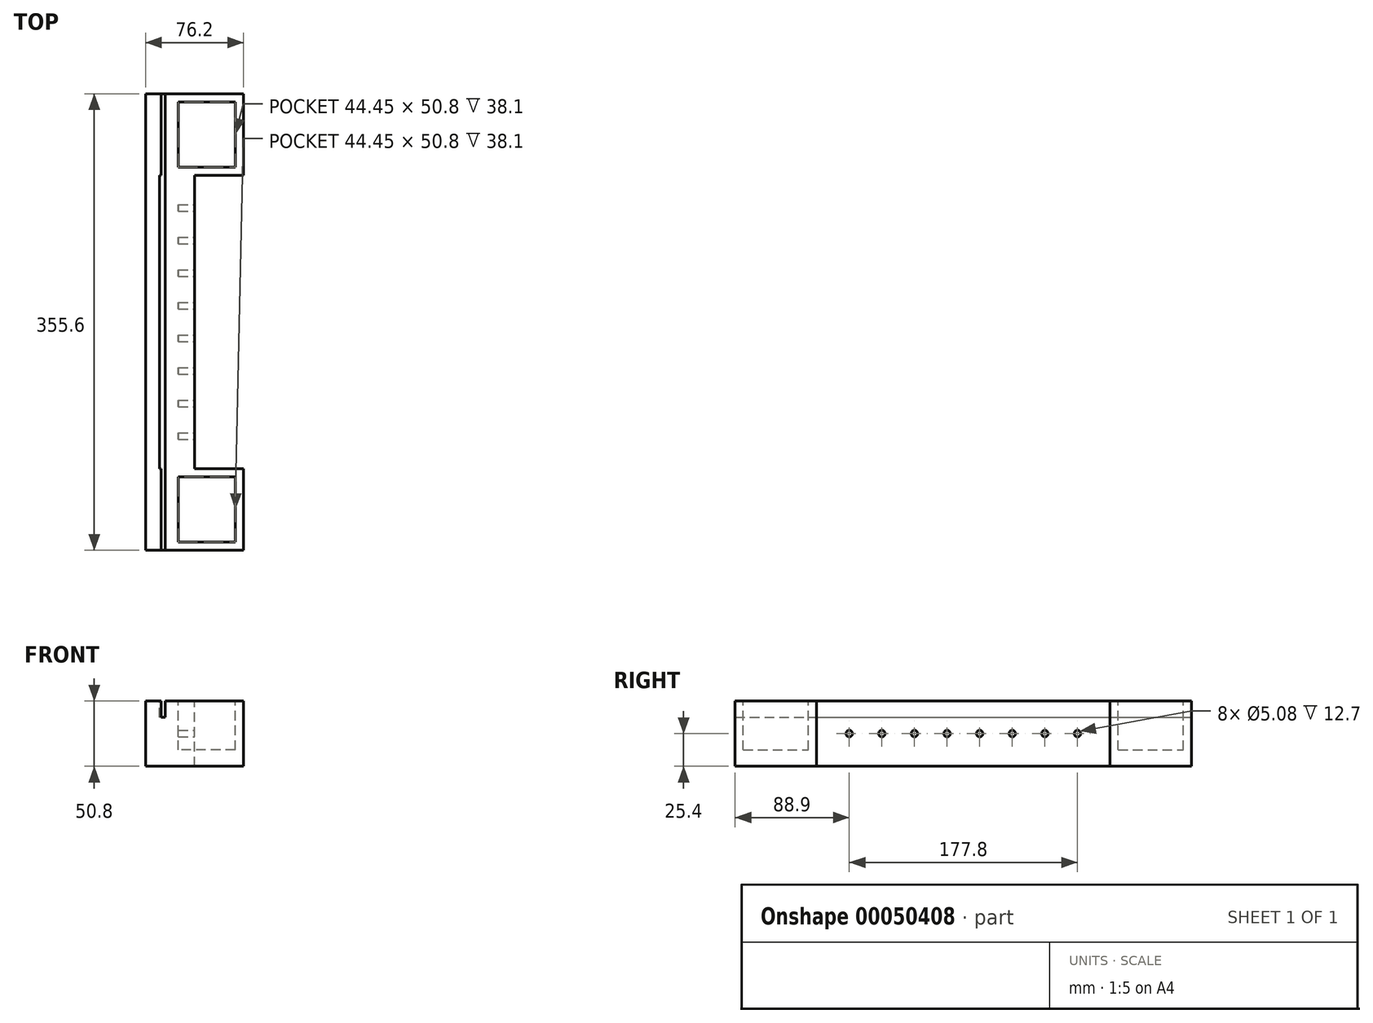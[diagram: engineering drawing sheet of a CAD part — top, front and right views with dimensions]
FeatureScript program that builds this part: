
annotation { "Feature Type Name" : "Feature", "Feature Type Description" : "" }
export const myFeature = defineFeature(function(context is Context, id is Id, definition is map)
    precondition{}
    {
        {
            var Q0;
            Q0=qCreatedBy(makeId("Right.planeOp"),FACE);
            var sketch = newSketch(context, id + "F0", { "sketchPlane" : qUnion([Q0])});
            skLineSegment(sketch, "E0.bottom", {"start": v(0, 0) * mm, "end": v(368.3, 0) * mm});
            skLineSegment(sketch, "E0.top", {"start": v(0, 50.8) * mm, "end": v(368.3, 50.8) * mm});
            skLineSegment(sketch, "E0.left", {"start": v(0, 0) * mm, "end": v(0, 50.8) * mm});
            skLineSegment(sketch, "E0.right", {"start": v(368.3, 0) * mm, "end": v(368.3, 50.8) * mm});
            skSolve(sketch);
        }
        {
            var Q0;
            Q0=makeQuery(id+"F0.imprint","IMPRINT",FACE,{"disambiguationData":[TD([[makeQuery(id+"F0.imprint","IMPRINT",EDGE,{"derivedFrom":sQuery(id+"F0.wireOp",EDGE,"E0.bottom")}),1.0]])]});
            extrude(context, id + "F1", {"entities" : qUnion([Q0]), "depth" : 38.1 * mm});
        }
        {
            var Q0;
            Q0=makeQuery(id+"F1.opExtrude","CAP_FACE",FACE,{"disambiguationData":[OSD([sQuery(id+"F0.wireOp",EDGE,"E0.bottom"),sQuery(id+"F0.wireOp",EDGE,"E0.top"),sQuery(id+"F0.wireOp",EDGE,"E0.left"),sQuery(id+"F0.wireOp",EDGE,"E0.right")])],"isStart":false});
            var sketch = newSketch(context, id + "F2", { "sketchPlane" : qUnion([Q0])});
            skLineSegment(sketch, "E1.bottom", {"start": v(0, 0) * mm, "end": v(76.2, 0) * mm});
            skLineSegment(sketch, "E1.top", {"start": v(0, 50.8) * mm, "end": v(76.2, 50.8) * mm});
            skLineSegment(sketch, "E1.left", {"start": v(0, 0) * mm, "end": v(0, 50.8) * mm});
            skLineSegment(sketch, "E1.right", {"start": v(76.2, 0) * mm, "end": v(76.2, 50.8) * mm});
            skLineSegment(sketch, "E2.bottom", {"start": v(368.3, 0) * mm, "end": v(292.1, 0) * mm});
            skLineSegment(sketch, "E2.top", {"start": v(368.3, 50.8) * mm, "end": v(292.1, 50.8) * mm});
            skLineSegment(sketch, "E2.left", {"start": v(368.3, 0) * mm, "end": v(368.3, 50.8) * mm});
            skLineSegment(sketch, "E2.right", {"start": v(292.1, 0) * mm, "end": v(292.1, 50.8) * mm});
            skSolve(sketch);
        }
        {
            var Q0;
            Q0=makeQuery(id+"F2.imprint","IMPRINT",FACE,{"disambiguationData":[TD([[makeQuery(id+"F2.imprint","IMPRINT",EDGE,{"derivedFrom":sQuery(id+"F2.wireOp",EDGE,"E1.bottom")}),1.0]])]});
            var Q1;
            Q1=makeQuery(id+"F2.imprint","IMPRINT",FACE,{"disambiguationData":[TD([[makeQuery(id+"F2.imprint","IMPRINT",EDGE,{"derivedFrom":sQuery(id+"F2.wireOp",EDGE,"E2.bottom")}),1.0]])]});
            extrude(context, id + "F3", {"entities" : qUnion([Q0, Q1]), "operationType" : NewBodyOperationType.ADD, "depth" : 38.1 * mm});
        }
        {
            var Q0;
            Q0=makeQuery(id+"F3.boolean.opBoolean","MERGE",FACE,{"derivedFrom":[makeQuery(id+"F1.opExtrude","SWEPT_FACE",FACE,{"disambiguationData":[OSD([sQuery(id+"F0.wireOp",EDGE,"E0.top")])]}),makeQuery(id+"F3.opExtrude","SWEPT_FACE",FACE,{"disambiguationData":[OSD([sQuery(id+"F2.wireOp",EDGE,"E1.top")])]}),makeQuery(id+"F3.opExtrude","SWEPT_FACE",FACE,{"disambiguationData":[OSD([sQuery(id+"F2.wireOp",EDGE,"E2.top")])]})]});
            var sketch = newSketch(context, id + "F4", { "sketchPlane" : qUnion([Q0])});
            skLineSegment(sketch, "E3.bottom", {"start": v(11.96, 6.35) * mm, "end": v(15.14, 6.35) * mm});
            skLineSegment(sketch, "E3.top", {"start": v(11.96, 69.85) * mm, "end": v(15.14, 69.85) * mm});
            skLineSegment(sketch, "E3.left", {"start": v(11.96, 6.35) * mm, "end": v(11.96, 69.85) * mm});
            skLineSegment(sketch, "E3.right", {"start": v(15.14, 6.35) * mm, "end": v(15.14, 69.85) * mm});
            skLineSegment(sketch, "E4.bottom", {"start": v(11.96, 298.45) * mm, "end": v(15.14, 298.45) * mm});
            skLineSegment(sketch, "E4.top", {"start": v(11.96, 361.95) * mm, "end": v(15.14, 361.95) * mm});
            skLineSegment(sketch, "E4.left", {"start": v(11.96, 298.45) * mm, "end": v(11.96, 361.95) * mm});
            skLineSegment(sketch, "E4.right", {"start": v(15.14, 298.45) * mm, "end": v(15.14, 361.95) * mm});
            skLineSegment(sketch, "E5.bottom", {"start": v(15.14, 69.85) * mm, "end": v(10.9, 69.85) * mm});
            skLineSegment(sketch, "E5.top", {"start": v(15.14, 298.45) * mm, "end": v(10.9, 298.45) * mm});
            skLineSegment(sketch, "E5.left", {"start": v(15.14, 69.85) * mm, "end": v(15.14, 298.45) * mm});
            skLineSegment(sketch, "E5.right", {"start": v(10.9, 69.85) * mm, "end": v(10.9, 298.45) * mm});
            skSolve(sketch);
        }
        {
            var Q0;
            Q0=makeQuery(id+"F4.imprint","IMPRINT",FACE,{"disambiguationData":[TD([[makeQuery(id+"F4.imprint","IMPRINT",EDGE,{"derivedFrom":sQuery(id+"F4.wireOp",EDGE,"E3.bottom")}),1.0]])]});
            var Q1;
            Q1=makeQuery(id+"F4.imprint","IMPRINT",FACE,{"disambiguationData":[TD([[makeQuery(id+"F4.imprint","IMPRINT",EDGE,{"derivedFrom":sQuery(id+"F4.wireOp",EDGE,"E4.top")}),-1.0]])]});
            var Q2;
            {var subQ3=sQuery(id+"F4.wireOp",EDGE,"E5.left");Q2=makeQuery(id+"F4.imprint","IMPRINT",FACE,{"disambiguationData":[TD([[makeQuery(id+"F4.imprint","IMPRINT",EDGE,{"derivedFrom":subQ3}),1.0]])]});}
            extrude(context, id + "F5", {"entities" : qUnion([Q0, Q1, Q2]), "operationType" : NewBodyOperationType.REMOVE, "oppositeDirection" : true, "depth" : 12.7 * mm});
        }
        {
            var Q0;
            Q0=makeQuery(id+"F3.boolean.opBoolean","MERGE",FACE,{"derivedFrom":[makeQuery(id+"F1.opExtrude","SWEPT_FACE",FACE,{"disambiguationData":[OSD([sQuery(id+"F0.wireOp",EDGE,"E0.top")])]}),makeQuery(id+"F3.opExtrude","SWEPT_FACE",FACE,{"disambiguationData":[OSD([sQuery(id+"F2.wireOp",EDGE,"E1.top")])]}),makeQuery(id+"F3.opExtrude","SWEPT_FACE",FACE,{"disambiguationData":[OSD([sQuery(id+"F2.wireOp",EDGE,"E2.top")])]})]});
            var sketch = newSketch(context, id + "F6", { "sketchPlane" : qUnion([Q0])});
            skLineSegment(sketch, "E6.0.0", {"start": v(0, 368.3) * mm, "end": v(0, 0) * mm});
            skLineSegment(sketch, "E6.0.1", {"start": v(0, 0) * mm, "end": v(76.2, 0) * mm});
            skLineSegment(sketch, "E6.0.2", {"start": v(76.2, 0) * mm, "end": v(76.2, 76.2) * mm});
            skLineSegment(sketch, "E6.0.3", {"start": v(76.2, 76.2) * mm, "end": v(38.1, 76.2) * mm});
            skLineSegment(sketch, "E6.0.4", {"start": v(38.1, 76.2) * mm, "end": v(38.1, 292.1) * mm});
            skLineSegment(sketch, "E6.0.5", {"start": v(38.1, 292.1) * mm, "end": v(76.2, 292.1) * mm});
            skLineSegment(sketch, "E6.0.6", {"start": v(76.2, 292.1) * mm, "end": v(76.2, 368.3) * mm});
            skLineSegment(sketch, "E6.0.7", {"start": v(76.2, 368.3) * mm, "end": v(0, 368.3) * mm});
            skLineSegment(sketch, "E7.bottom", {"start": v(69.85, 12.7) * mm, "end": v(25.4, 12.7) * mm});
            skLineSegment(sketch, "E7.top", {"start": v(69.85, 63.5) * mm, "end": v(25.4, 63.5) * mm});
            skLineSegment(sketch, "E7.left", {"start": v(69.85, 12.7) * mm, "end": v(69.85, 63.5) * mm});
            skLineSegment(sketch, "E7.right", {"start": v(25.4, 12.7) * mm, "end": v(25.4, 63.5) * mm});
            skLineSegment(sketch, "E8.bottom", {"start": v(69.85, 304.8) * mm, "end": v(25.4, 304.8) * mm});
            skLineSegment(sketch, "E8.top", {"start": v(69.85, 355.6) * mm, "end": v(25.4, 355.6) * mm});
            skLineSegment(sketch, "E8.left", {"start": v(69.85, 304.8) * mm, "end": v(69.85, 355.6) * mm});
            skLineSegment(sketch, "E8.right", {"start": v(25.4, 304.8) * mm, "end": v(25.4, 355.6) * mm});
            skSolve(sketch);
        }
        {
            var Q0;
            Q0=makeQuery(id+"F6.imprint","IMPRINT",FACE,{"disambiguationData":[TD([[makeQuery(id+"F6.imprint","IMPRINT",EDGE,{"derivedFrom":sQuery(id+"F6.wireOp",EDGE,"E7.bottom")}),-1.0]])]});
            var Q1;
            Q1=makeQuery(id+"F6.imprint","IMPRINT",FACE,{"disambiguationData":[TD([[makeQuery(id+"F6.imprint","IMPRINT",EDGE,{"derivedFrom":sQuery(id+"F6.wireOp",EDGE,"E8.bottom")}),-1.0]])]});
            extrude(context, id + "F7", {"entities" : qUnion([Q0, Q1]), "operationType" : NewBodyOperationType.REMOVE, "oppositeDirection" : true, "depth" : 38.1 * mm});
        }
        {
            var Q0;
            Q0=makeQuery(id+"F1.opExtrude","CAP_FACE",FACE,{"disambiguationData":[OSD([sQuery(id+"F0.wireOp",EDGE,"E0.bottom"),sQuery(id+"F0.wireOp",EDGE,"E0.top"),sQuery(id+"F0.wireOp",EDGE,"E0.left"),sQuery(id+"F0.wireOp",EDGE,"E0.right")])],"isStart":false});
            var sketch = newSketch(context, id + "F8", { "sketchPlane" : qUnion([Q0])});
            skCircle(sketch, "E9", {"center": v(95.25, 25.4) * mm, "radius": 2.54 * mm});
            skCircle(sketch, "E10.1.0.0", {"center": v(120.65, 25.4) * mm, "radius": 2.54 * mm});
            skCircle(sketch, "E10.2.0.0", {"center": v(146.05, 25.4) * mm, "radius": 2.54 * mm});
            skCircle(sketch, "E10.3.0.0", {"center": v(171.45, 25.4) * mm, "radius": 2.54 * mm});
            skCircle(sketch, "E10.4.0.0", {"center": v(196.85, 25.4) * mm, "radius": 2.54 * mm});
            skCircle(sketch, "E10.5.0.0", {"center": v(222.25, 25.4) * mm, "radius": 2.54 * mm});
            skCircle(sketch, "E10.6.0.0", {"center": v(247.65, 25.4) * mm, "radius": 2.54 * mm});
            skLineSegment(sketch, "E10.direction1", {"start": v(95.25, 25.4) * mm, "end": v(120.65, 25.4) * mm, "construction": true});
            skCircle(sketch, "E11.0.7.0", {"center": v(273.05, 25.4) * mm, "radius": 2.54 * mm});
            skSolve(sketch);
        }
        {
            var Q0;
            Q0=makeQuery(id+"F8.imprint","IMPRINT",FACE,{"disambiguationData":[TD([[makeQuery(id+"F8.imprint","IMPRINT",EDGE,{"derivedFrom":sQuery(id+"F8.wireOp",EDGE,"E10.1.0.0")}),1.0]])]});
            var Q1;
            Q1=makeQuery(id+"F8.imprint","IMPRINT",FACE,{"disambiguationData":[TD([[makeQuery(id+"F8.imprint","IMPRINT",EDGE,{"derivedFrom":sQuery(id+"F8.wireOp",EDGE,"E10.2.0.0")}),1.0]])]});
            var Q2;
            Q2=makeQuery(id+"F8.imprint","IMPRINT",FACE,{"disambiguationData":[TD([[makeQuery(id+"F8.imprint","IMPRINT",EDGE,{"derivedFrom":sQuery(id+"F8.wireOp",EDGE,"E10.3.0.0")}),1.0]])]});
            var Q3;
            Q3=makeQuery(id+"F8.imprint","IMPRINT",FACE,{"disambiguationData":[TD([[makeQuery(id+"F8.imprint","IMPRINT",EDGE,{"derivedFrom":sQuery(id+"F8.wireOp",EDGE,"E10.4.0.0")}),1.0]])]});
            var Q4;
            Q4=makeQuery(id+"F8.imprint","IMPRINT",FACE,{"disambiguationData":[TD([[makeQuery(id+"F8.imprint","IMPRINT",EDGE,{"derivedFrom":sQuery(id+"F8.wireOp",EDGE,"E10.5.0.0")}),1.0]])]});
            var Q5;
            Q5=makeQuery(id+"F8.imprint","IMPRINT",FACE,{"disambiguationData":[TD([[makeQuery(id+"F8.imprint","IMPRINT",EDGE,{"derivedFrom":sQuery(id+"F8.wireOp",EDGE,"E10.6.0.0")}),1.0]])]});
            var Q6;
            Q6=makeQuery(id+"F8.imprint","IMPRINT",FACE,{"disambiguationData":[TD([[makeQuery(id+"F8.imprint","IMPRINT",EDGE,{"derivedFrom":sQuery(id+"F8.wireOp",EDGE,"E9")}),1.0]])]});
            var Q7;
            Q7=makeQuery(id+"F8.imprint","IMPRINT",FACE,{"disambiguationData":[TD([[makeQuery(id+"F8.imprint","IMPRINT",EDGE,{"derivedFrom":sQuery(id+"F8.wireOp",EDGE,"E11.0.7.0")}),1.0]])]});
            extrude(context, id + "F9", {"entities" : qUnion([Q0, Q1, Q2, Q3, Q4, Q5, Q6, Q7]), "operationType" : NewBodyOperationType.REMOVE, "oppositeDirection" : true, "depth" : 12.7 * mm});
        }
        {
            var Q0;
            Q0=makeQuery(id+"F3.boolean.opBoolean","MERGE",FACE,{"derivedFrom":[makeQuery(id+"F1.opExtrude","SWEPT_FACE",FACE,{"disambiguationData":[OSD([sQuery(id+"F0.wireOp",EDGE,"E0.top")])]}),makeQuery(id+"F3.opExtrude","SWEPT_FACE",FACE,{"disambiguationData":[OSD([sQuery(id+"F2.wireOp",EDGE,"E1.top")])]}),makeQuery(id+"F3.opExtrude","SWEPT_FACE",FACE,{"disambiguationData":[OSD([sQuery(id+"F2.wireOp",EDGE,"E2.top")])]})]});
            var sketch = newSketch(context, id + "F10", { "sketchPlane" : qUnion([Q0])});
            skLineSegment(sketch, "E12.bottom", {"start": v(0, 0) * mm, "end": v(76.2, 0) * mm});
            skLineSegment(sketch, "E12.top", {"start": v(0, 6.35) * mm, "end": v(76.2, 6.35) * mm});
            skLineSegment(sketch, "E12.left", {"start": v(0, 0) * mm, "end": v(0, 6.35) * mm});
            skLineSegment(sketch, "E12.right", {"start": v(76.2, 0) * mm, "end": v(76.2, 6.35) * mm});
            skLineSegment(sketch, "E13.bottom", {"start": v(38.1, 76.2) * mm, "end": v(76.2, 76.2) * mm});
            skLineSegment(sketch, "E13.top", {"start": v(38.1, 69.85) * mm, "end": v(76.2, 69.85) * mm});
            skLineSegment(sketch, "E13.left", {"start": v(38.1, 76.2) * mm, "end": v(38.1, 69.85) * mm});
            skLineSegment(sketch, "E13.right", {"start": v(76.2, 76.2) * mm, "end": v(76.2, 69.85) * mm});
            skLineSegment(sketch, "E14.bottom", {"start": v(0, 368.3) * mm, "end": v(76.2, 368.3) * mm});
            skLineSegment(sketch, "E14.top", {"start": v(0, 361.95) * mm, "end": v(76.2, 361.95) * mm});
            skLineSegment(sketch, "E14.left", {"start": v(0, 368.3) * mm, "end": v(0, 361.95) * mm});
            skLineSegment(sketch, "E14.right", {"start": v(76.2, 368.3) * mm, "end": v(76.2, 361.95) * mm});
            skLineSegment(sketch, "E15.bottom", {"start": v(38.1, 292.1) * mm, "end": v(76.2, 292.1) * mm});
            skLineSegment(sketch, "E15.top", {"start": v(38.1, 298.45) * mm, "end": v(76.2, 298.45) * mm});
            skLineSegment(sketch, "E15.left", {"start": v(38.1, 292.1) * mm, "end": v(38.1, 298.45) * mm});
            skLineSegment(sketch, "E15.right", {"start": v(76.2, 292.1) * mm, "end": v(76.2, 298.45) * mm});
            skSolve(sketch);
        }
        {
            var Q0;
            Q0 = qSketchRegion(id + "F10", true);
            extrude(context, id + "F11", {"entities" : qUnion([Q0]), "operationType" : NewBodyOperationType.REMOVE, "oppositeDirection" : true, "depth" : 76.2 * mm});
        }
    });
